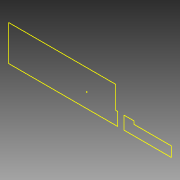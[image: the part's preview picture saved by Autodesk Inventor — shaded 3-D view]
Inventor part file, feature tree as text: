
AUTODESK INVENTOR PART (.ipt)
format: ipt  version: 2014 (Build 180170000, 170)  size: 79,360 bytes
history: native  units: in
note: dims shown in document units (in); Inventor stores cm internally (conversion verified against a paired STEP export)
features: reference x8, extrude x1, sketch x1
ambient origin geometry x8: Origin, YZ Plane, XZ Plane, XY Plane, X Axis, Y Axis, Z Axis, Center Point
bodies: Solid1 (feature_tree)
feature tree (10):
  extrude  "Extrusion1"  [1 undecoded]
  sketch  "Sketch2"  dims[d0=0.0039in d1=0.0in]
  reference  "Reference4"
  reference  "Reference5"
  reference  "Reference6"
  reference  "Reference7"
  reference  "Reference8"
  reference  "Reference9"
  reference  "Reference10"
  reference  "Reference11"
note: 1 required parameter value undecoded (feature->parameter linkage not recoverable at this tier; creation-order binding heuristic only, values carry confidence <= 0.55)
